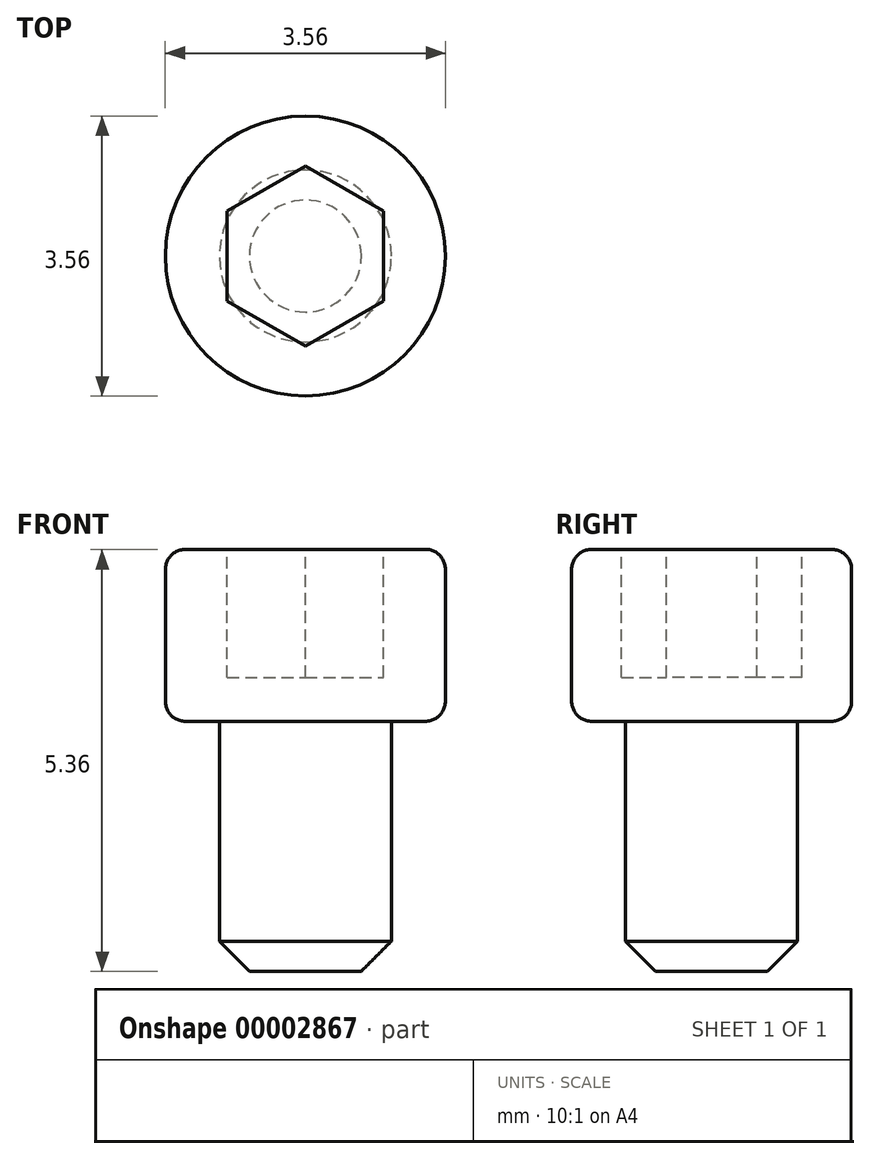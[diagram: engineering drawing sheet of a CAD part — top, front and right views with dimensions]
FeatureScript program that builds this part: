
annotation { "Feature Type Name" : "Feature", "Feature Type Description" : "" }
export const myFeature = defineFeature(function(context is Context, id is Id, definition is map)
    precondition{}
    {
        {
            var Q0;
            Q0=qCreatedBy(makeId("Top.planeOp"),FACE);
            var sketch = newSketch(context, id + "F0", { "sketchPlane" : qUnion([Q0])});
            skCircle(sketch, "E0", {"center": v(0, 0) * mm, "radius": 1.1 * mm});
            skSolve(sketch);
        }
        {
            var Q0;
            Q0=makeQuery(id+"F0.imprint","IMPRINT",FACE,{"disambiguationData":[TD([[makeQuery(id+"F0.imprint","IMPRINT",EDGE,{"derivedFrom":sQuery(id+"F0.wireOp",EDGE,"E0")}),1.0]])]});
            extrude(context, id + "F1", {"entities" : qUnion([Q0]), "oppositeDirection" : true, "depth" : 3.17 * mm});
        }
        {
            var Q0;
            Q0=qCreatedBy(makeId("Top.planeOp"),FACE);
            var sketch = newSketch(context, id + "F2", { "sketchPlane" : qUnion([Q0])});
            skCircle(sketch, "E1", {"center": v(0, 0) * mm, "radius": 1.78 * mm});
            skSolve(sketch);
        }
        {
            var Q0;
            Q0=qSketchRegion(id+"F2",true);
            extrude(context, id + "F3", {"entities" : qUnion([Q0]), "operationType" : NewBodyOperationType.ADD, "depth" : 2.18 * mm});
        }
        {
            var Q0;
            Q0=makeQuery(id+"F3.opExtrude","CAP_FACE",FACE,{"disambiguationData":[OSD([sQuery(id+"F2.wireOp",EDGE,"E1")])],"isStart":false});
            var sketch = newSketch(context, id + "F4", { "sketchPlane" : qUnion([Q0])});
            skCircle(sketch, "E2.cCircle", {"center": v(0, 0) * mm, "radius": 1 * mm, "construction": true});
            skLineSegment(sketch, "E2.0", {"start": v(1, 0.57) * mm, "end": v(1, -0.57) * mm});
            skLineSegment(sketch, "E2.1", {"start": v(1, -0.57) * mm, "end": v(0, -1.15) * mm});
            skLineSegment(sketch, "E2.2", {"start": v(0, -1.15) * mm, "end": v(-1, -0.57) * mm});
            skLineSegment(sketch, "E2.3", {"start": v(-1, -0.57) * mm, "end": v(-1, 0.57) * mm});
            skLineSegment(sketch, "E2.4", {"start": v(-1, 0.57) * mm, "end": v(0, 1.15) * mm});
            skLineSegment(sketch, "E2.5", {"start": v(0, 1.15) * mm, "end": v(1, 0.57) * mm});
            skPoint(sketch, "E2.0.midPoint", {"position": v(1, 0) * mm});
            skSolve(sketch);
        }
        {
            var Q0;
            Q0=makeQuery(id+"F4.imprint","IMPRINT",FACE,{"disambiguationData":[TD([[makeQuery(id+"F4.imprint","IMPRINT",EDGE,{"derivedFrom":sQuery(id+"F4.wireOp",EDGE,"E2.0")}),-1.0]])]});
            extrude(context, id + "F5", {"entities" : qUnion([Q0]), "operationType" : NewBodyOperationType.REMOVE, "oppositeDirection" : true, "depth" : 1.63 * mm});
        }
        {
            var Q0;
            Q0=makeQuery(id+"F1.opExtrude","CAP_EDGE",EDGE,{"disambiguationData":[OSD([sQuery(id+"F0.wireOp",EDGE,"E0")])],"isStart":false});
            chamfer(context, id + "F6", {"entities" : qUnion([Q0]), "chamferType" : ChamferType.OFFSET_ANGLE, "width" : 0.38 * mm, "oppositeDirection" : false, "angle" : 45 * degree, "tangentPropagation" : true});
        }
        {
            var Q0;
            Q0=qCreatedBy(makeId("Top.planeOp"),FACE);
            cPlane(context, id + "F7", {"entities" : qUnion([Q0]), "cplaneType" : CPlaneType.OFFSET, "offset" : ((1 / 56) * 2) * mm, "oppositeDirection" : true, "width" : 152.4 * mm, "height" : 152.4 * mm});
        }
        {
            var Q0;
            Q0=qCreatedBy(id+"F7.planeOp",FACE);
            var sketch = newSketch(context, id + "F8", { "sketchPlane" : qUnion([Q0])});
            skCircle(sketch, "E3", {"center": v(0, 0) * mm, "radius": 0.8 * mm});
            skSolve(sketch);
        }
        {
            var Q0;
            Q0=sQuery(id+"F8.wireOp",EDGE,"E3");
            var Q1;
            Q1=makeQuery(id+"F6.opChamfer","BLEND_FACE",FACE,{"disambiguationData":[OSD([sQuery(id+"F0.wireOp",EDGE,"E0")])]});
            extrude(context, id + "F9", {"bodyType" : ToolBodyType.SURFACE, "surfaceEntities" : qUnion([Q0]), "endBound" : BoundingType.UP_TO_SURFACE, "oppositeDirection" : true, "endBoundEntityFace" : qUnion([Q1]), "depth" : 25.4 * mm});
        }
        {
            var Q0;
            Q0=makeQuery(id+"F3.opExtrude","CAP_EDGE",EDGE,{"disambiguationData":[OSD([sQuery(id+"F2.wireOp",EDGE,"E1")])],"isStart":false});
            var Q1;
            Q1=makeQuery(id+"F3.opExtrude","CAP_EDGE",EDGE,{"disambiguationData":[OSD([sQuery(id+"F2.wireOp",EDGE,"E1")])],"isStart":true});
            fillet(context, id + "F10", {"entities" : qUnion([Q0, Q1]), "radius" : 0.25 * mm, "tangentPropagation" : true, "allowEdgeOverflow" : false});
        }
    });
